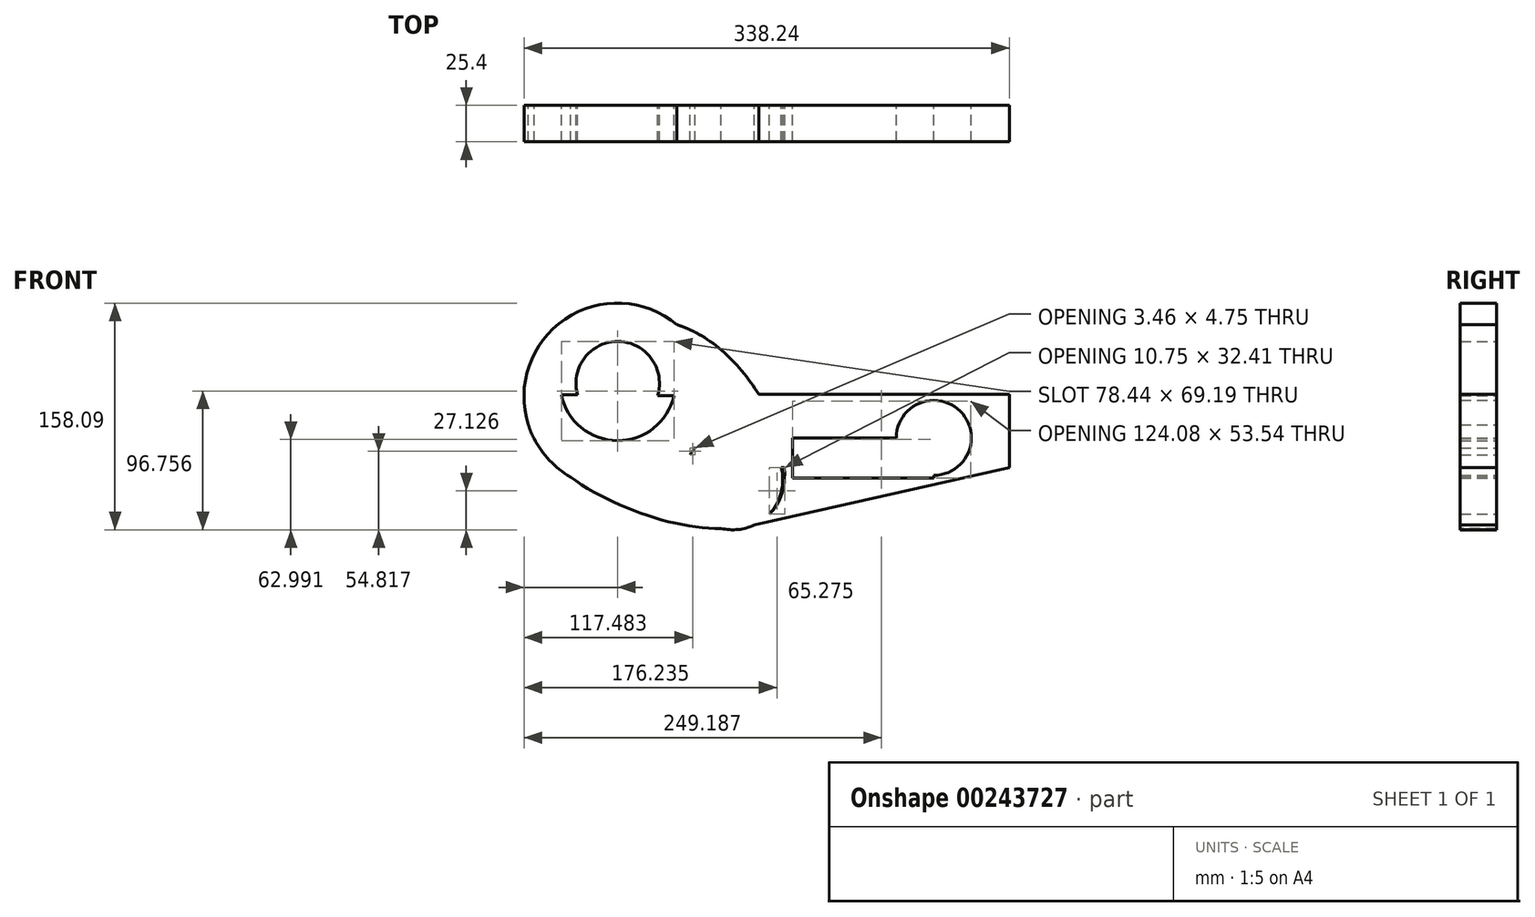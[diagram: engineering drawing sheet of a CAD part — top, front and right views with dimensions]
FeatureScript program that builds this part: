
annotation { "Feature Type Name" : "Feature", "Feature Type Description" : "" }
export const myFeature = defineFeature(function(context is Context, id is Id, definition is map)
    precondition{}
    {
        {
            var Q0;
            Q0=qCreatedBy(makeId("Front.planeOp"),FACE);
            var sketch = newSketch(context, id + "F0", { "sketchPlane" : qUnion([Q0])});
            skArc(sketch, "E0", {"start": v(-27.38, 0) * mm, "mid": v(6.32, -43.33) * mm, "end": v(40, 0) * mm});
            skArc(sketch, "E1", {"start": v(40, 0) * mm, "mid": v(6.32, 25.88) * mm, "end": v(-27.38, 0) * mm});
            skCircle(sketch, "E2", {"center": v(-74.23, 49.75) * mm, "radius": 65 * mm});
            skFitSpline(sketch, "E3", {"points": [v(-32.66, 99.73) * mm, v(31.62, -32.4) * mm, v(-136.1, 29.8) * mm, v(-32.66, 99.73) * mm]});
            skArc(sketch, "E4", {"start": v(-113.19, 50.8) * mm, "mid": v(-74.18, 18.83) * mm, "end": v(-34.75, 50.28) * mm});
            skLineSegment(sketch, "E5", {"start": v(-113.19, 50.8) * mm, "end": v(-34.75, 50.28) * mm});
            skLineSegment(sketch, "E6.bottom", {"start": v(24.39, 51.1) * mm, "end": v(199, 51.1) * mm});
            skLineSegment(sketch, "E6.top", {"start": v(24.39, 0) * mm, "end": v(199, 0) * mm});
            skLineSegment(sketch, "E6.left", {"start": v(24.39, 51.1) * mm, "end": v(24.39, 0) * mm});
            skLineSegment(sketch, "E6.right", {"start": v(199, 51.1) * mm, "end": v(199, 0) * mm});
            skLineSegment(sketch, "E7", {"start": v(6.32, -43.33) * mm, "end": v(199, 0) * mm});
            skLineSegment(sketch, "E8.bottom", {"start": v(47.9, 20.8) * mm, "end": v(146.35, 20.8) * mm});
            skLineSegment(sketch, "E8.top", {"start": v(47.9, -7.1) * mm, "end": v(146.35, -7.1) * mm});
            skLineSegment(sketch, "E8.left", {"start": v(47.9, 20.8) * mm, "end": v(47.9, -7.1) * mm});
            skLineSegment(sketch, "E8.right", {"start": v(146.35, 20.8) * mm, "end": v(146.35, -7.1) * mm});
            skCircle(sketch, "E9", {"center": v(146.35, 20.8) * mm, "radius": 26.14 * mm});
            skCircle(sketch, "E10", {"center": v(-73.9, 58.94) * mm, "radius": 29.08 * mm});
            skLineSegment(sketch, "E11", {"start": v(-49.37, 109.82) * mm, "end": v(-15.56, 92.03) * mm});
            skSolve(sketch);
        }
        {
            var Q0;
            {var subQ0=sQuery(id+"F0.wireOp",EDGE,"E7");var subQ1=sQuery(id+"F0.wireOp",EDGE,"E0");var subQ2=makeQuery(id+"F0.imprint","INTERSECT",VERTEX,{"disambiguationData":[OD(0.0)],"derivedFrom":[subQ1,subQ0]});Q0=makeQuery(id+"F0.imprint","IMPRINT",FACE,{"disambiguationData":[TD([[makeQuery(id+"F0.imprint","IMPRINT",EDGE,{"disambiguationData":[TD([[subQ2,-1.0]])],"derivedFrom":subQ1}),1.0]])]});}
            var Q1;
            {var subQ0=sQuery(id+"F0.wireOp",EDGE,"E11");var subQ1=sQuery(id+"F0.wireOp",EDGE,"E2");var subQ2=makeQuery(id+"F0.imprint","INTERSECT",VERTEX,{"disambiguationData":[OD(0.0)],"derivedFrom":[subQ1,subQ0]});Q1=makeQuery(id+"F0.imprint","IMPRINT",FACE,{"disambiguationData":[TD([[makeQuery(id+"F0.imprint","IMPRINT",EDGE,{"disambiguationData":[TD([[subQ2,1.0]])],"derivedFrom":subQ1}),1.0]])]});}
            var Q2;
            {var subQ0=sQuery(id+"F0.wireOp",EDGE,"E3");var subQ1=sQuery(id+"F0.wireOp",EDGE,"E2");var subQ2=makeQuery(id+"F0.imprint","INTERSECT",VERTEX,{"disambiguationData":[OD(0.0)],"derivedFrom":[subQ1,subQ0]});Q2=makeQuery(id+"F0.imprint","IMPRINT",FACE,{"disambiguationData":[TD([[makeQuery(id+"F0.imprint","IMPRINT",EDGE,{"disambiguationData":[TD([[subQ2,-1.0]])],"derivedFrom":subQ1}),-1.0]])]});}
            var Q3;
            {var subQ0=sQuery(id+"F0.wireOp",EDGE,"E3");var subQ1=sQuery(id+"F0.wireOp",EDGE,"E2");var subQ2=makeQuery(id+"F0.imprint","INTERSECT",VERTEX,{"disambiguationData":[OD(1.0)],"derivedFrom":[subQ1,subQ0]});Q3=makeQuery(id+"F0.imprint","IMPRINT",FACE,{"disambiguationData":[TD([[makeQuery(id+"F0.imprint","IMPRINT",EDGE,{"disambiguationData":[TD([[subQ2,-1.0]])],"derivedFrom":subQ1}),1.0]])]});}
            var Q4;
            {var subQ0=sQuery(id+"F0.wireOp",EDGE,"E11");var subQ1=sQuery(id+"F0.wireOp",EDGE,"E3");var subQ2=makeQuery(id+"F0.imprint","INTERSECT",VERTEX,{"disambiguationData":[OD(0.0)],"derivedFrom":[subQ1,subQ0]});Q4=makeQuery(id+"F0.imprint","IMPRINT",FACE,{"disambiguationData":[TD([[makeQuery(id+"F0.imprint","IMPRINT",EDGE,{"disambiguationData":[TD([[subQ2,1.0]])],"derivedFrom":subQ1}),-1.0]])]});}
            var Q5;
            {var subQ0=sQuery(id+"F0.wireOp",EDGE,"E1");var subQ1=sQuery(id+"F0.wireOp",EDGE,"E0");var subQ2=makeQuery(id+"F0.imprint","INTERSECT",VERTEX,{"derivedFrom":[subQ1,subQ0]});Q5=makeQuery(id+"F0.imprint","IMPRINT",FACE,{"disambiguationData":[TD([[makeQuery(id+"F0.imprint","IMPRINT",EDGE,{"disambiguationData":[TD([[subQ2,-1.0]])],"derivedFrom":subQ1}),-1.0]])]});}
            var Q6;
            {var subQ0=sQuery(id+"F0.wireOp",EDGE,"E11");var subQ1=sQuery(id+"F0.wireOp",EDGE,"E2");var subQ2=makeQuery(id+"F0.imprint","INTERSECT",VERTEX,{"disambiguationData":[OD(1.0)],"derivedFrom":[subQ1,subQ0]});Q6=makeQuery(id+"F0.imprint","IMPRINT",FACE,{"disambiguationData":[TD([[makeQuery(id+"F0.imprint","IMPRINT",EDGE,{"disambiguationData":[TD([[subQ2,1.0]])],"derivedFrom":subQ1}),-1.0]])]});}
            var Q7;
            {var subQ0=sQuery(id+"F0.wireOp",EDGE,"E7");var subQ1=sQuery(id+"F0.wireOp",EDGE,"E0");var subQ2=makeQuery(id+"F0.imprint","INTERSECT",VERTEX,{"disambiguationData":[OD(0.0)],"derivedFrom":[subQ1,subQ0]});Q7=makeQuery(id+"F0.imprint","IMPRINT",FACE,{"disambiguationData":[TD([[makeQuery(id+"F0.imprint","IMPRINT",EDGE,{"disambiguationData":[TD([[subQ2,1.0]])],"derivedFrom":subQ1}),1.0]])]});}
            var Q8;
            {var subQ0=sQuery(id+"F0.wireOp",EDGE,"E11");var subQ1=sQuery(id+"F0.wireOp",EDGE,"E2");var subQ2=makeQuery(id+"F0.imprint","INTERSECT",VERTEX,{"disambiguationData":[OD(1.0)],"derivedFrom":[subQ1,subQ0]});Q8=makeQuery(id+"F0.imprint","IMPRINT",FACE,{"disambiguationData":[TD([[makeQuery(id+"F0.imprint","IMPRINT",EDGE,{"disambiguationData":[TD([[subQ2,1.0]])],"derivedFrom":subQ1}),1.0]])]});}
            var Q9;
            {var subQ1=sQuery(id+"F0.wireOp",EDGE,"E1");var subQ3=sQuery(id+"F0.wireOp",EDGE,"E6.left");var subQ4=makeQuery(id+"F0.imprint","INTERSECT",VERTEX,{"derivedFrom":[subQ1,subQ3]});Q9=makeQuery(id+"F0.imprint","IMPRINT",FACE,{"disambiguationData":[TD([[makeQuery(id+"F0.imprint","IMPRINT",EDGE,{"disambiguationData":[TD([[subQ4,1.0]])],"derivedFrom":subQ1}),-1.0]])]});}
            var Q10;
            {var subQ4=sQuery(id+"F0.wireOp",EDGE,"E6.bottom");Q10=makeQuery(id+"F0.imprint","IMPRINT",FACE,{"disambiguationData":[TD([[makeQuery(id+"F0.imprint","IMPRINT",EDGE,{"derivedFrom":subQ4}),-1.0]])]});}
            var Q11;
            {var subQ7=sQuery(id+"F0.wireOp",EDGE,"E8.top");Q11=makeQuery(id+"F0.imprint","IMPRINT",FACE,{"disambiguationData":[TD([[makeQuery(id+"F0.imprint","IMPRINT",EDGE,{"derivedFrom":subQ7}),-1.0]])]});}
            var Q12;
            {var subQ5=sQuery(id+"F0.wireOp",EDGE,"E6.left");var subQ6=sQuery(id+"F0.wireOp",EDGE,"E1");var subQ7=makeQuery(id+"F0.imprint","INTERSECT",VERTEX,{"derivedFrom":[subQ6,subQ5]});Q12=makeQuery(id+"F0.imprint","IMPRINT",FACE,{"disambiguationData":[TD([[makeQuery(id+"F0.imprint","IMPRINT",EDGE,{"disambiguationData":[TD([[subQ7,-1.0]])],"derivedFrom":subQ6}),-1.0]])]});}
            var Q13;
            {var subQ9=sQuery(id+"F0.wireOp",EDGE,"E4");Q13=makeQuery(id+"F0.imprint","IMPRINT",FACE,{"disambiguationData":[TD([[makeQuery(id+"F0.imprint","IMPRINT",EDGE,{"derivedFrom":subQ9}),-1.0]])]});}
            var Q14;
            {var subQ0=sQuery(id+"F0.wireOp",EDGE,"E6.top");var subQ3=sQuery(id+"F0.wireOp",EDGE,"E6.left");var subQ5=makeQuery(id+"F0.imprint","INTERSECT",VERTEX,{"derivedFrom":[subQ0,subQ3]});Q14=makeQuery(id+"F0.imprint","IMPRINT",FACE,{"disambiguationData":[TD([[makeQuery(id+"F0.imprint","IMPRINT",EDGE,{"disambiguationData":[TD([[subQ5,1.0]])],"derivedFrom":subQ3}),1.0]])]});}
            var Q15;
            {var subQ0=sQuery(id+"F0.wireOp",EDGE,"E1");var subQ1=sQuery(id+"F0.wireOp",EDGE,"E0");var subQ2=makeQuery(id+"F0.imprint","INTERSECT",VERTEX,{"derivedFrom":[subQ1,subQ0]});Q15=makeQuery(id+"F0.imprint","IMPRINT",FACE,{"disambiguationData":[TD([[makeQuery(id+"F0.imprint","IMPRINT",EDGE,{"disambiguationData":[TD([[subQ2,-1.0]])],"derivedFrom":subQ1}),1.0]])]});}
            extrude(context, id + "F1", {"entities" : qUnion([Q0, Q1, Q2, Q3, Q4, Q5, Q6, Q7, Q8, Q9, Q10, Q11, Q12, Q13, Q14, Q15]), "depth" : 25.4 * mm});
        }
    });
